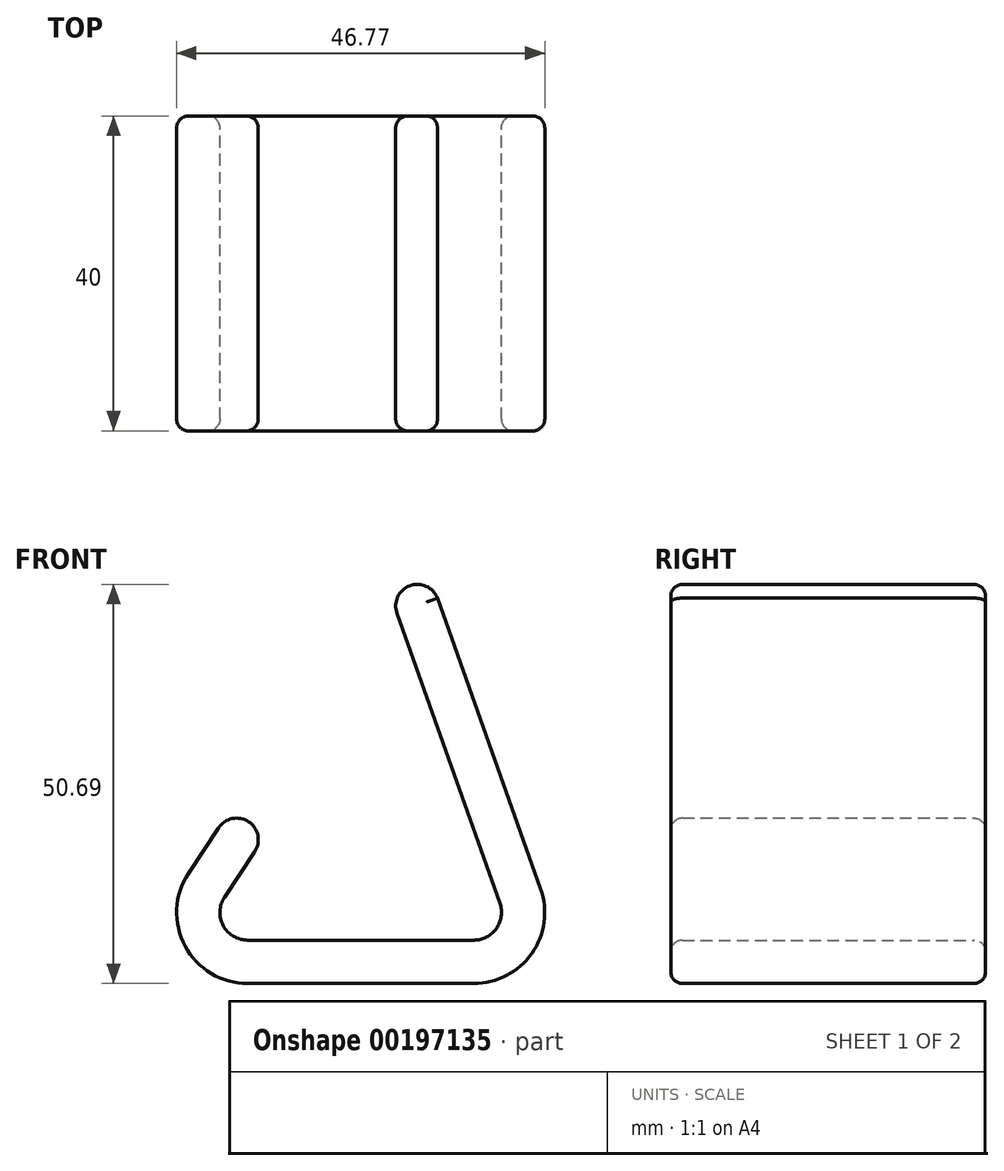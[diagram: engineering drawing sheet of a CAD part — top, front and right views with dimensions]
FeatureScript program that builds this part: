
annotation { "Feature Type Name" : "Feature", "Feature Type Description" : "" }
export const myFeature = defineFeature(function(context is Context, id is Id, definition is map)
    precondition{}
    {
        {
            var Q0;
            Q0=qCreatedBy(makeId("Front.planeOp"),FACE);
            var sketch = newSketch(context, id + "F0", { "sketchPlane" : qUnion([Q0])});
            skLineSegment(sketch, "E0", {"start": v(6.54, 0) * mm, "end": v(35.27, 0) * mm});
            skLineSegment(sketch, "E1", {"start": v(38.58, 4.69) * mm, "end": v(25.51, 41.52) * mm});
            skLineSegment(sketch, "E2", {"start": v(3.6, 5.45) * mm, "end": v(7.44, 11.24) * mm});
            skPoint(sketch, "E3.visualSharp", {"position": v(0, 0) * mm});
            skArc(sketch, "E3.filletArc", {"start": v(3.6, 5.45) * mm, "mid": v(3.44, 1.85) * mm, "end": v(6.54, 0) * mm});
            skPoint(sketch, "E4.visualSharp", {"position": v(40.25, 0) * mm});
            skArc(sketch, "E4.filletArc", {"start": v(35.27, 0) * mm, "mid": v(38.14, 1.49) * mm, "end": v(38.58, 4.69) * mm});
            skLineSegment(sketch, "E5.0", {"start": v(-0.98, 8.49) * mm, "end": v(2.85, 14.27) * mm});
            skLineSegment(sketch, "E5.1", {"start": v(43.77, 6.53) * mm, "end": v(30.66, 43.45) * mm});
            skArc(sketch, "E5.2", {"start": v(35.27, -5.5) * mm, "mid": v(42.64, -1.69) * mm, "end": v(43.77, 6.53) * mm});
            skLineSegment(sketch, "E5.3", {"start": v(6.54, -5.5) * mm, "end": v(35.27, -5.5) * mm});
            skArc(sketch, "E5.4", {"start": v(-0.98, 8.49) * mm, "mid": v(-1.4, -0.75) * mm, "end": v(6.54, -5.5) * mm});
            skArc(sketch, "E6", {"start": v(25.51, 41.52) * mm, "mid": v(27.14, 45.01) * mm, "end": v(30.66, 43.45) * mm});
            skArc(sketch, "E7", {"start": v(2.85, 14.27) * mm, "mid": v(6.66, 15.05) * mm, "end": v(7.44, 11.24) * mm});
            skSolve(sketch);
        }
        {
            var Q0;
            Q0 = qSketchRegion(id + "F0", true);
            extrude(context, id + "F1", {"entities" : qUnion([Q0]), "endBound" : BoundingType.SYMMETRIC, "depth" : 40 * mm});
        }
        {
            var Q0;
            Q0=makeQuery(id+"F1.opExtrude","CAP_FACE",FACE,{"disambiguationData":[OSD([sQuery(id+"F0.wireOp",EDGE,"E0"),sQuery(id+"F0.wireOp",EDGE,"E1"),sQuery(id+"F0.wireOp",EDGE,"E2"),sQuery(id+"F0.wireOp",EDGE,"E3.filletArc"),sQuery(id+"F0.wireOp",EDGE,"E4.filletArc"),sQuery(id+"F0.wireOp",EDGE,"E5.0"),sQuery(id+"F0.wireOp",EDGE,"E5.1"),sQuery(id+"F0.wireOp",EDGE,"E5.2"),sQuery(id+"F0.wireOp",EDGE,"E5.3"),sQuery(id+"F0.wireOp",EDGE,"E5.4"),sQuery(id+"F0.wireOp",EDGE,"E6"),sQuery(id+"F0.wireOp",EDGE,"E7")])],"isStart":true});
            var Q1;
            Q1=makeQuery(id+"F1.opExtrude","CAP_FACE",FACE,{"disambiguationData":[OSD([sQuery(id+"F0.wireOp",EDGE,"E0"),sQuery(id+"F0.wireOp",EDGE,"E1"),sQuery(id+"F0.wireOp",EDGE,"E2"),sQuery(id+"F0.wireOp",EDGE,"E3.filletArc"),sQuery(id+"F0.wireOp",EDGE,"E4.filletArc"),sQuery(id+"F0.wireOp",EDGE,"E5.0"),sQuery(id+"F0.wireOp",EDGE,"E5.1"),sQuery(id+"F0.wireOp",EDGE,"E5.2"),sQuery(id+"F0.wireOp",EDGE,"E5.3"),sQuery(id+"F0.wireOp",EDGE,"E5.4"),sQuery(id+"F0.wireOp",EDGE,"E6"),sQuery(id+"F0.wireOp",EDGE,"E7")])],"isStart":false});
            fillet(context, id + "F2", {"entities" : qUnion([Q0, Q1]), "radius" : 1.5 * mm, "tangentPropagation" : true, "allowEdgeOverflow" : false});
        }
    });
